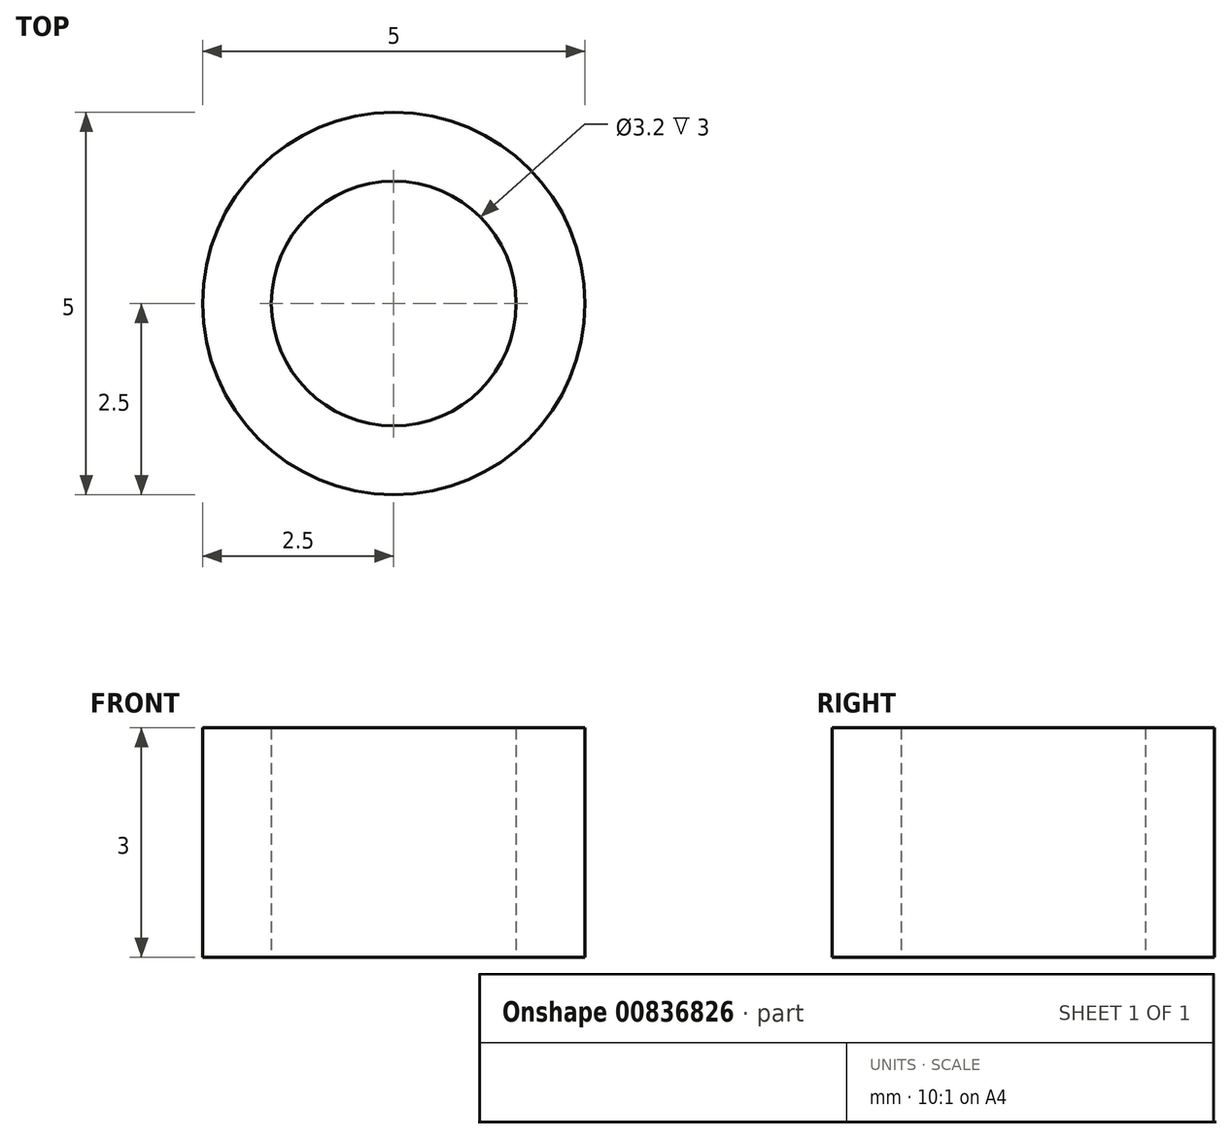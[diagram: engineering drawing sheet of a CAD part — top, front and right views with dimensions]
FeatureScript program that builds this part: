
annotation { "Feature Type Name" : "Feature", "Feature Type Description" : "" }
export const myFeature = defineFeature(function(context is Context, id is Id, definition is map)
    precondition{}
    {
        {
            var Q0;
            Q0=qCreatedBy(makeId("Top.planeOp"),FACE);
            var sketch = newSketch(context, id + "F0", { "sketchPlane" : qUnion([Q0])});
            skCircle(sketch, "E0", {"center": v(0, 0) * mm, "radius": 1.6 * mm});
            skCircle(sketch, "E1", {"center": v(0, 0) * mm, "radius": 2.5 * mm});
            skSolve(sketch);
        }
        {
            var Q0;
            Q0 = qSketchRegion(id + "F0", true);
            extrude(context, id + "F1", {"entities" : qUnion([Q0]), "depth" : 3 * mm, "offsetDistance" : 25 * mm});
        }
    });
